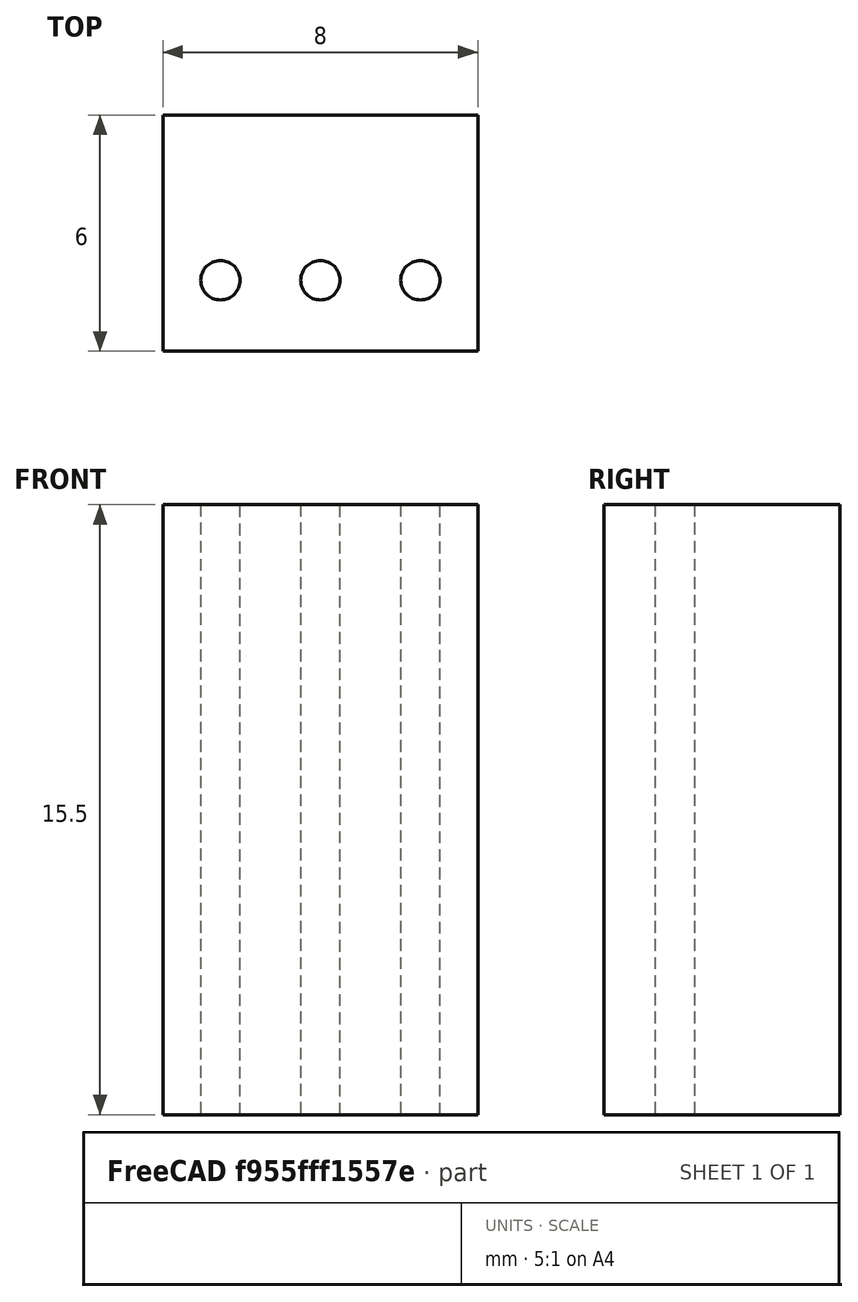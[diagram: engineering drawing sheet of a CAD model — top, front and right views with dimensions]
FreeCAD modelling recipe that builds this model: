
FCSTD DOCUMENT  (FreeCAD 0.20R29603 (Git))
Label: IR_Sockel
License: All rights reserved
LicenseURL: http://en.wikipedia.org/wiki/All_rights_reserved
objects: Sketcher::SketchObject×1, PartDesign::Pad×1, PartDesign::Body×1
note: 4 computed .brp shape members not serialized (recipe doc carries the construction recipe); baked Part::Feature solids carry a one-line shape summary decoded from their .brp

FEATURE [Sketcher::SketchObject] Sketch
  FullyConstrained = true
  MapMode = 5
  Support = -> [XY_Plane]
  sketch-geometry (7):
    g0: LineSegment StartX=0 StartY=0 StartZ=0 EndX=8 EndY=0 EndZ=0
    g1: LineSegment StartX=8 StartY=0 StartZ=0 EndX=8 EndY=6 EndZ=0
    g2: LineSegment StartX=8 StartY=6 StartZ=0 EndX=0 EndY=6 EndZ=0
    g3: LineSegment StartX=0 StartY=6 StartZ=0 EndX=0 EndY=0 EndZ=0
    g4: Circle CenterX=1.46 CenterY=1.8 CenterZ=0 NormalX=0 NormalY=0 NormalZ=1 AngleXU=0 Radius=0.5
    g5: Circle CenterX=4 CenterY=1.8 CenterZ=0 NormalX=0 NormalY=0 NormalZ=1 AngleXU=0 Radius=0.5
    g6: Circle CenterX=6.54 CenterY=1.8 CenterZ=0 NormalX=0 NormalY=0 NormalZ=1 AngleXU=0 Radius=0.5
  constraints (20):
    c: Coincident(g0,g1)
    c: Coincident(g1,g2)
    c: Coincident(g2,g3)
    c: Coincident(g3,g0)
    c: Horizontal(g0)
    c: Horizontal(g2)
    c: Vertical(g1)
    c: Vertical(g3)
    c: Coincident(g0,g-1)
    c: DistanceY(g3,g3) = 6
    c: DistanceX(g2,g2) = 8
    c: Equal(g4,g5)
    c: Equal(g4,g6)
    c: Diameter(g4) = 1
    c: Horizontal(g5,g4)
    c: Horizontal(g4,g6)
    c: DistanceX(g4,g5) = 2.54
    c: DistanceX(g5,g6) = 2.54
    c: DistanceY(g0,g5) = 1.8
    c: DistanceX(g0,g5) = 4
FEATURE [PartDesign::Pad] Pad
  Direction = (0,0,1)
  Length = 15.5
  Length2 = 10
  Profile = -> Sketch
  ReferenceAxis = -> Sketch [N_Axis]
  Refine = true
  Type = 0
FEATURE [PartDesign::Body] Body
  Group = -> [Sketch,Pad]
  Origin = -> Origin
  Tip = -> Pad
